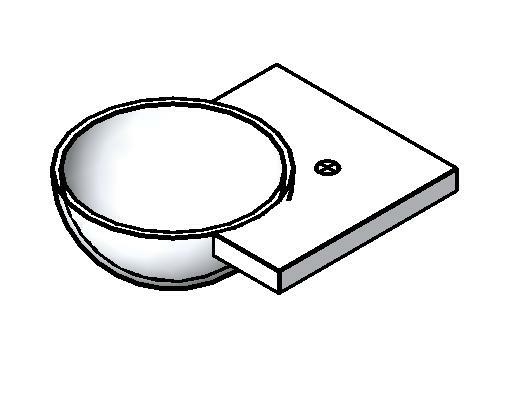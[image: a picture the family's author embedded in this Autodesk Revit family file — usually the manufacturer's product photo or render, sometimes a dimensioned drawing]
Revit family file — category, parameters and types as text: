
# Revit family: Deca_Lavatorio suspenso de canto_L.76_Canto
name_source: partatom
category: Plumbing Fixtures
revit_build: Autodesk Revit 2013 (Build: 20120221_2030(x64)
units: mm (PartAtom-declared; Revit-internal decimal feet)

## types (2) — shared parameters
Acompanha o Produto = Acompanha dois kits para fixação: (SP.07.01)
Aprovado por = Contino/quattroD
Assembly Code = D2010300
Atendimento ao Cliente = 0800-0117073
Criado por = Contino/quattroD
Default Elevation = 800 mm  [stored 2.62467 ft]
Description = Lavatório suspenso
Diâmetro Ponto de Esgoto = 40 mm  [stored 0.131234 ft]
Flow Pressure = 0.00 psi
Informações Complementares = Acompanha fixação
Linha = Cubas suspensas
Louça/Metais = Louça
Manufacturer = Deca
Material = Deca_Fireclay
Norma = ABNT NBR 15097-1: 2011 / ABNT NBR 15097-2: 2011
Peso Liquido (Kg) = 11
Produto = Lavatório Master de Canto
Raio Ponto de Esgoto = 20 mm  [stored 0.0656168 ft]
Segmento = Luxo
URL = www.deca.com.br/produtos
Variações de COR = Branco (L.76.17); Ébano (L.76.95).
Vendido Separadamente = Sifão para lavatório: Cromado: (1680.C.100.112), Dourado (1680.D.100.112).   Slim: Cromado 100.112), Dourado (1684.D.100.112).  Quadra: Cromado (1685.C.100.112). Articulado: Cromado (1682.C.100.112). Válvulas de escoamentos compatíveis: Luxo: Cromado (1601.C), Branco (1601.E.BR). Click: Cromado (1601.C.CLI). Competitivo: Cromado (1602.C), Dourado (1602.D); Tampão plástico: Cromado (1602.C.PLA). Dois kits para fixação: (SP.07.01) (Utilizar 3 parafusos)
zero-valued in all types: WFU

## per-type parameters (varying)
| type | Cuba | Código | Model |
| L.76.17_Branco Gelo GE17 | Deca GE17 Branco Gelo Cerâmica | L.76.17 | L.76.17 |
| L.76.95_Ébano EB95 | Deca EB95 Ébano Cerâmica | L.76.95 | L.76.95 |

note: [stored X ft] marks values corroborated as IEEE doubles in the binary element streams (Revit-internal decimal feet)

## geometry (parser evidence)
native form markers: Blend x4, Sweep x1
no freeform markers — native parametric forms only
